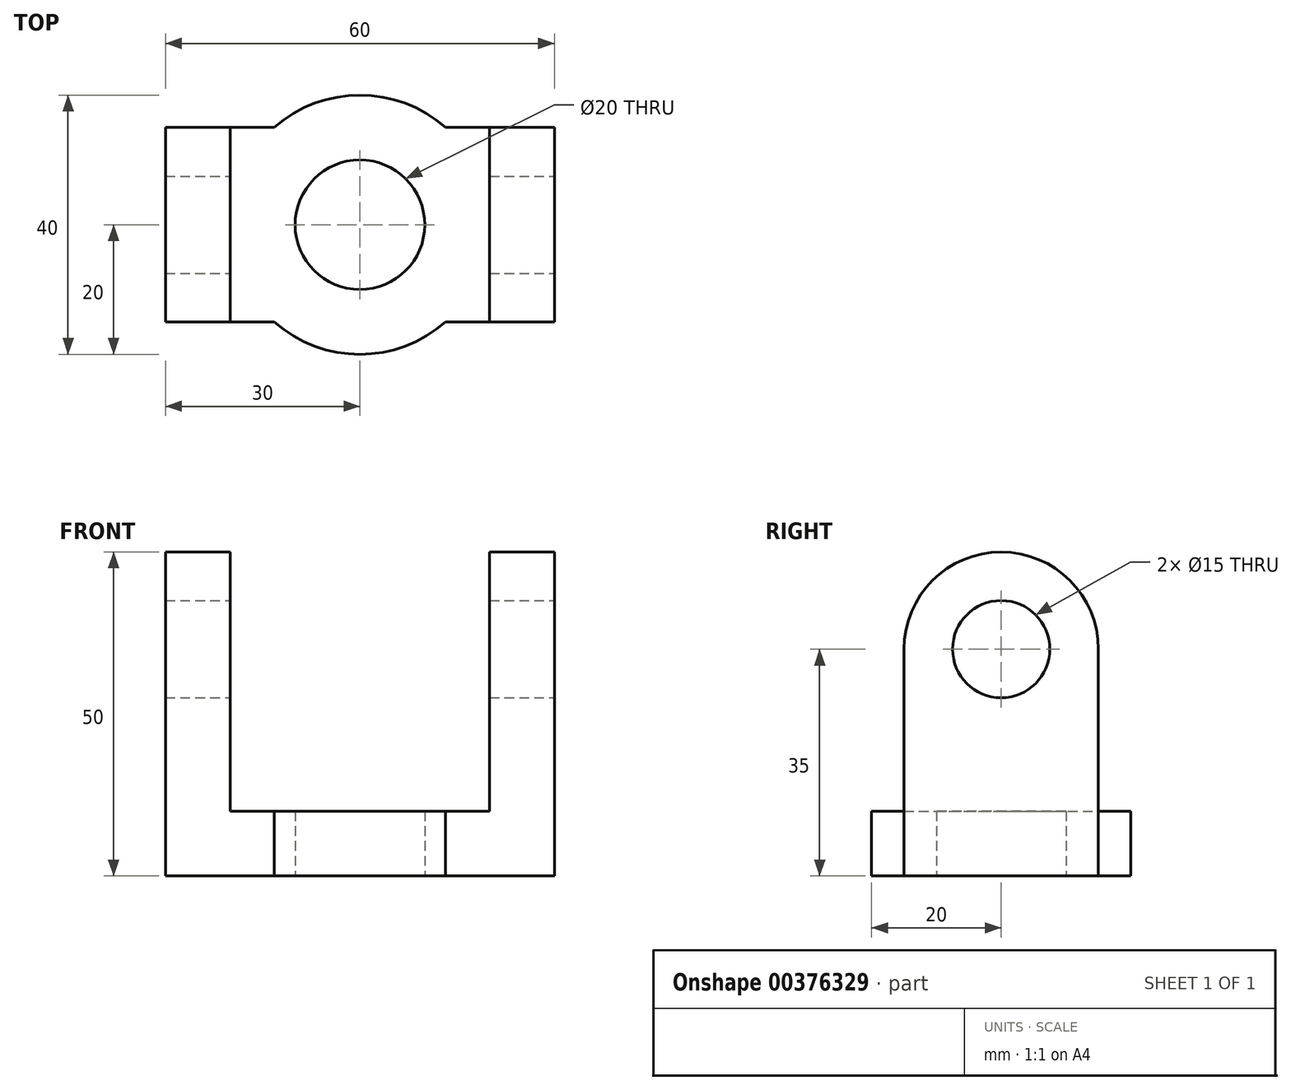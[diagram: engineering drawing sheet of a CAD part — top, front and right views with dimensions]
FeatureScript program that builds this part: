
annotation { "Feature Type Name" : "Feature", "Feature Type Description" : "" }
export const myFeature = defineFeature(function(context is Context, id is Id, definition is map)
    precondition{}
    {
        {
            var Q0;
            Q0=qCreatedBy(makeId("Top.planeOp"),FACE);
            var sketch = newSketch(context, id + "F0", { "sketchPlane" : qUnion([Q0])});
            skCircle(sketch, "E0", {"center": v(0, 0) * mm, "radius": 20 * mm});
            skCircle(sketch, "E1", {"center": v(0, 0) * mm, "radius": 10 * mm});
            skLineSegment(sketch, "E2", {"start": v(-38.74, 0) * mm, "end": v(33.89, 0) * mm, "construction": true});
            skLineSegment(sketch, "E3", {"start": v(-30, 0) * mm, "end": v(-30, 15) * mm});
            skLineSegment(sketch, "E4", {"start": v(-30, 15) * mm, "end": v(30, 15) * mm});
            skLineSegment(sketch, "E5", {"start": v(30, 15) * mm, "end": v(30, 0) * mm});
            skLineSegment(sketch, "E6", {"start": v(30, 0) * mm, "end": v(-30, 0) * mm});
            skLineSegment(sketch, "E7.MirrorCS", {"start": v(-30, 0) * mm, "end": v(-30, -15) * mm});
            skLineSegment(sketch, "E8.MirrorCS", {"start": v(-30, -15) * mm, "end": v(30, -15) * mm});
            skLineSegment(sketch, "E9.MirrorCS", {"start": v(30, -15) * mm, "end": v(30, 0) * mm});
            skSolve(sketch);
        }
        {
            var Q0;
            {var subQ0=sQuery(id+"F0.wireOp",EDGE,"E4");var subQ1=sQuery(id+"F0.wireOp",EDGE,"E0");var subQ2=makeQuery(id+"F0.imprint","INTERSECT",VERTEX,{"disambiguationData":[OD(0.0)],"derivedFrom":[subQ1,subQ0]});Q0=makeQuery(id+"F0.imprint","IMPRINT",FACE,{"disambiguationData":[TD([[makeQuery(id+"F0.imprint","IMPRINT",EDGE,{"disambiguationData":[TD([[subQ2,-1.0]])],"derivedFrom":subQ1}),1.0]])]});}
            var Q1;
            {var subQ4=sQuery(id+"F0.wireOp",EDGE,"E4");var subQ5=sQuery(id+"F0.wireOp",EDGE,"E0");var subQ8=makeQuery(id+"F0.imprint","INTERSECT",VERTEX,{"disambiguationData":[OD(0.0)],"derivedFrom":[subQ5,subQ4]});Q1=makeQuery(id+"F0.imprint","IMPRINT",FACE,{"disambiguationData":[TD([[makeQuery(id+"F0.imprint","IMPRINT",EDGE,{"disambiguationData":[TD([[subQ8,1.0]])],"derivedFrom":subQ5}),1.0]])]});}
            var Q2;
            {var subQ5=sQuery(id+"F0.wireOp",EDGE,"E3");Q2=makeQuery(id+"F0.imprint","IMPRINT",FACE,{"disambiguationData":[TD([[makeQuery(id+"F0.imprint","IMPRINT",EDGE,{"derivedFrom":subQ5}),-1.0]])]});}
            var Q3;
            {var subQ5=sQuery(id+"F0.wireOp",EDGE,"E7.MirrorCS");Q3=makeQuery(id+"F0.imprint","IMPRINT",FACE,{"disambiguationData":[TD([[makeQuery(id+"F0.imprint","IMPRINT",EDGE,{"derivedFrom":subQ5}),1.0]])]});}
            var Q4;
            {var subQ1=sQuery(id+"F0.wireOp",EDGE,"E0");var subQ5=sQuery(id+"F0.wireOp",EDGE,"E8.MirrorCS");var subQ6=makeQuery(id+"F0.imprint","INTERSECT",VERTEX,{"disambiguationData":[OD(0.0)],"derivedFrom":[subQ1,subQ5]});Q4=makeQuery(id+"F0.imprint","IMPRINT",FACE,{"disambiguationData":[TD([[makeQuery(id+"F0.imprint","IMPRINT",EDGE,{"disambiguationData":[TD([[subQ6,1.0]])],"derivedFrom":subQ1}),1.0]])]});}
            var Q5;
            {var subQ5=sQuery(id+"F0.wireOp",EDGE,"E9.MirrorCS");Q5=makeQuery(id+"F0.imprint","IMPRINT",FACE,{"disambiguationData":[TD([[makeQuery(id+"F0.imprint","IMPRINT",EDGE,{"derivedFrom":subQ5}),1.0]])]});}
            var Q6;
            {var subQ5=sQuery(id+"F0.wireOp",EDGE,"E5");Q6=makeQuery(id+"F0.imprint","IMPRINT",FACE,{"disambiguationData":[TD([[makeQuery(id+"F0.imprint","IMPRINT",EDGE,{"derivedFrom":subQ5}),-1.0]])]});}
            var Q7;
            {var subQ0=sQuery(id+"F0.wireOp",EDGE,"E8.MirrorCS");var subQ1=sQuery(id+"F0.wireOp",EDGE,"E0");var subQ2=makeQuery(id+"F0.imprint","INTERSECT",VERTEX,{"disambiguationData":[OD(0.0)],"derivedFrom":[subQ1,subQ0]});Q7=makeQuery(id+"F0.imprint","IMPRINT",FACE,{"disambiguationData":[TD([[makeQuery(id+"F0.imprint","IMPRINT",EDGE,{"disambiguationData":[TD([[subQ2,-1.0]])],"derivedFrom":subQ1}),1.0]])]});}
            extrude(context, id + "F1", {"entities" : qUnion([Q0, Q1, Q2, Q3, Q4, Q5, Q6, Q7]), "depth" : 10 * mm});
        }
        {
            var Q0;
            Q0=makeQuery(id+"F1.opExtrude","SWEPT_FACE",FACE,{"disambiguationData":[OSD([sQuery(id+"F0.wireOp",EDGE,"E3"),sQuery(id+"F0.wireOp",EDGE,"E7.MirrorCS")])]});
            var sketch = newSketch(context, id + "F2", { "sketchPlane" : qUnion([Q0])});
            skLineSegment(sketch, "E10", {"start": v(-15, 10) * mm, "end": v(-15, 35) * mm});
            skLineSegment(sketch, "E11", {"start": v(15, 10) * mm, "end": v(15, 35) * mm});
            skArc(sketch, "E12", {"start": v(15, 35) * mm, "mid": v(0, 50) * mm, "end": v(-15, 35) * mm});
            skLineSegment(sketch, "E13", {"start": v(-15, 10) * mm, "end": v(15, 10) * mm});
            skSolve(sketch);
        }
        {
            var Q0;
            Q0 = qSketchRegion(id + "F2", true);
            extrude(context, id + "F3", {"entities" : qUnion([Q0]), "operationType" : NewBodyOperationType.ADD, "oppositeDirection" : true, "depth" : 10 * mm});
        }
        {
            var Q0;
            Q0=makeQuery(id+"F1.opExtrude","SWEPT_FACE",FACE,{"disambiguationData":[OSD([sQuery(id+"F0.wireOp",EDGE,"E5"),sQuery(id+"F0.wireOp",EDGE,"E9.MirrorCS")])]});
            var sketch = newSketch(context, id + "F4", { "sketchPlane" : qUnion([Q0])});
            skLineSegment(sketch, "E14", {"start": v(-15, 10) * mm, "end": v(-15, 35) * mm});
            skLineSegment(sketch, "E15", {"start": v(15, 10) * mm, "end": v(15, 35) * mm});
            skArc(sketch, "E16", {"start": v(15, 35) * mm, "mid": v(0, 50) * mm, "end": v(-15, 35) * mm});
            skLineSegment(sketch, "E17", {"start": v(-15, 10) * mm, "end": v(15, 10) * mm});
            skSolve(sketch);
        }
        {
            var Q0;
            Q0 = qSketchRegion(id + "F4", true);
            extrude(context, id + "F5", {"entities" : qUnion([Q0]), "operationType" : NewBodyOperationType.ADD, "oppositeDirection" : true, "depth" : 10 * mm});
        }
        {
            var Q0;
            Q0=makeQuery(id+"F5.boolean.opBoolean","MERGE",FACE,{"derivedFrom":[makeQuery(id+"F1.opExtrude","SWEPT_FACE",FACE,{"disambiguationData":[OSD([sQuery(id+"F0.wireOp",EDGE,"E5"),sQuery(id+"F0.wireOp",EDGE,"E9.MirrorCS")])]}),makeQuery(id+"F5.opExtrude","CAP_FACE",FACE,{"disambiguationData":[OSD([sQuery(id+"F4.wireOp",EDGE,"E14"),sQuery(id+"F4.wireOp",EDGE,"E15"),sQuery(id+"F4.wireOp",EDGE,"E16"),sQuery(id+"F4.wireOp",EDGE,"E17")])],"isStart":true})]});
            var sketch = newSketch(context, id + "F6", { "sketchPlane" : qUnion([Q0])});
            skCircle(sketch, "E18", {"center": v(0, 35) * mm, "radius": 7.5 * mm});
            skSolve(sketch);
        }
        {
            var Q0;
            Q0 = qSketchRegion(id + "F6", true);
            extrude(context, id + "F7", {"entities" : qUnion([Q0]), "operationType" : NewBodyOperationType.REMOVE, "endBound" : BoundingType.THROUGH_ALL, "oppositeDirection" : true, "depth" : 25 * mm});
        }
    });
